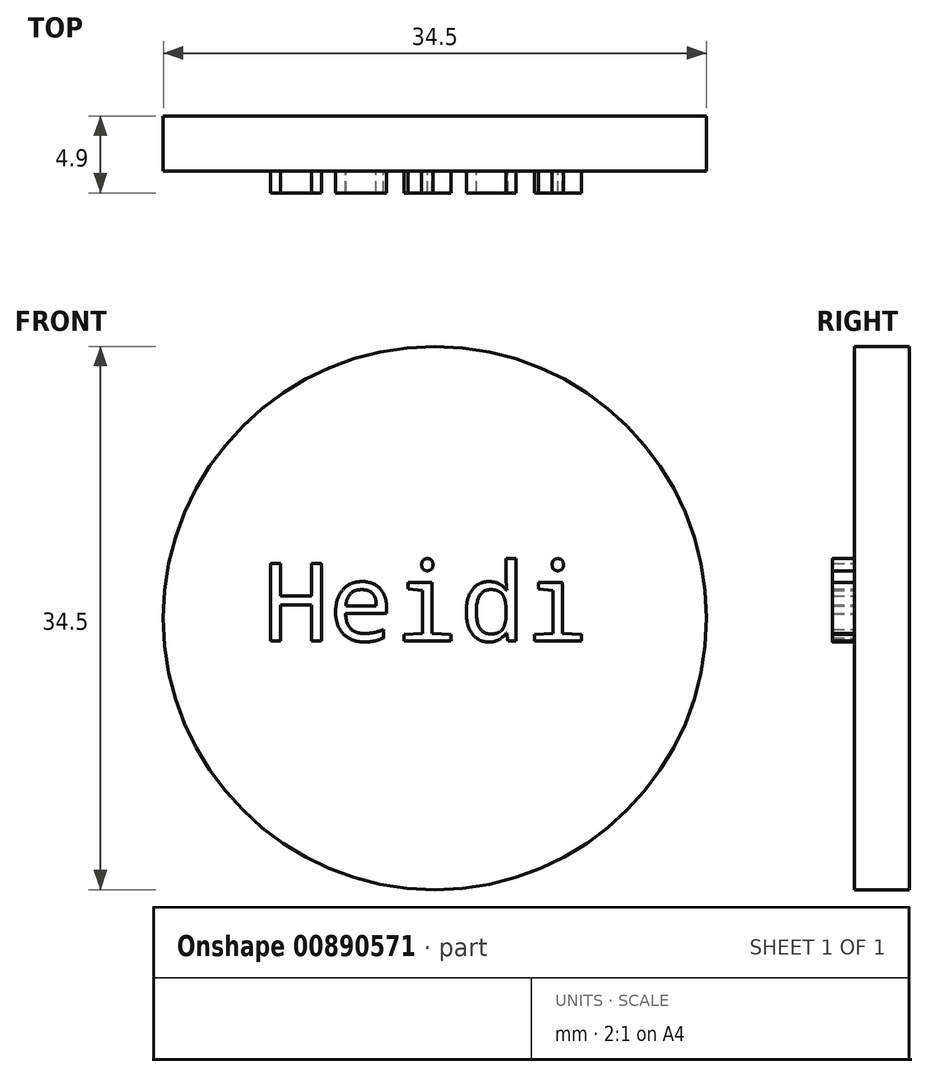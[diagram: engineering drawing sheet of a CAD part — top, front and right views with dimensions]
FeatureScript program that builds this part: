
annotation { "Feature Type Name" : "Feature", "Feature Type Description" : "" }
export const myFeature = defineFeature(function(context is Context, id is Id, definition is map)
    precondition{}
    {
        {
            var Q0;
            Q0=qCreatedBy(makeId("Front.planeOp"),FACE);
            var sketch = newSketch(context, id + "F0", { "sketchPlane" : qUnion([Q0])});
            skCircle(sketch, "E0", {"center": v(0, 0) * mm, "radius": 17.25 * mm});
            skSolve(sketch);
        }
        {
            var Q0;
            Q0 = qSketchRegion(id + "F0", true);
            extrude(context, id + "F1", {"entities" : qUnion([Q0]), "depth" : 3.5 * mm, "offsetDistance" : 25 * mm});
        }
        {
            var Q0;
            Q0=makeQuery(id+"F1.opExtrude","CAP_FACE",FACE,{"disambiguationData":[OSD([sQuery(id+"F0.wireOp",EDGE,"E0")])],"isStart":false});
            var sketch = newSketch(context, id + "F2", { "sketchPlane" : qUnion([Q0])});
            skText(sketch, "E1", { "text": "Heidi", "fontName": "DroidSansMono.ttf"});
            const initialGuessF2  = {"E1": [-0.0109, -0.00145, 1, 0, 0.00497]};
            skSetInitialGuess(sketch, initialGuessF2);
            skSolve(sketch);
        }
        {
            var Q0;
            Q0=makeQuery(id+"F2.imprint","IMPRINT",FACE,{"disambiguationData":[TD([[makeQuery(id+"F2.imprint","IMPRINT",EDGE,{"derivedFrom":sQuery(id+"F2.wireOp",EDGE,"E1.sketch_text.stroke-0")}),1.0]])]});
            var sketch = newSketch(context, id + "F3", { "sketchPlane" : qUnion([Q0])});
            skSolve(sketch);
        }
        {
            var Q0;
            Q0 = qSketchRegion(id + "F2", true);
            extrude(context, id + "F4", {"entities" : qUnion([Q0]), "operationType" : NewBodyOperationType.ADD, "depth" : 1.4 * mm, "offsetDistance" : 25 * mm});
        }
    });
